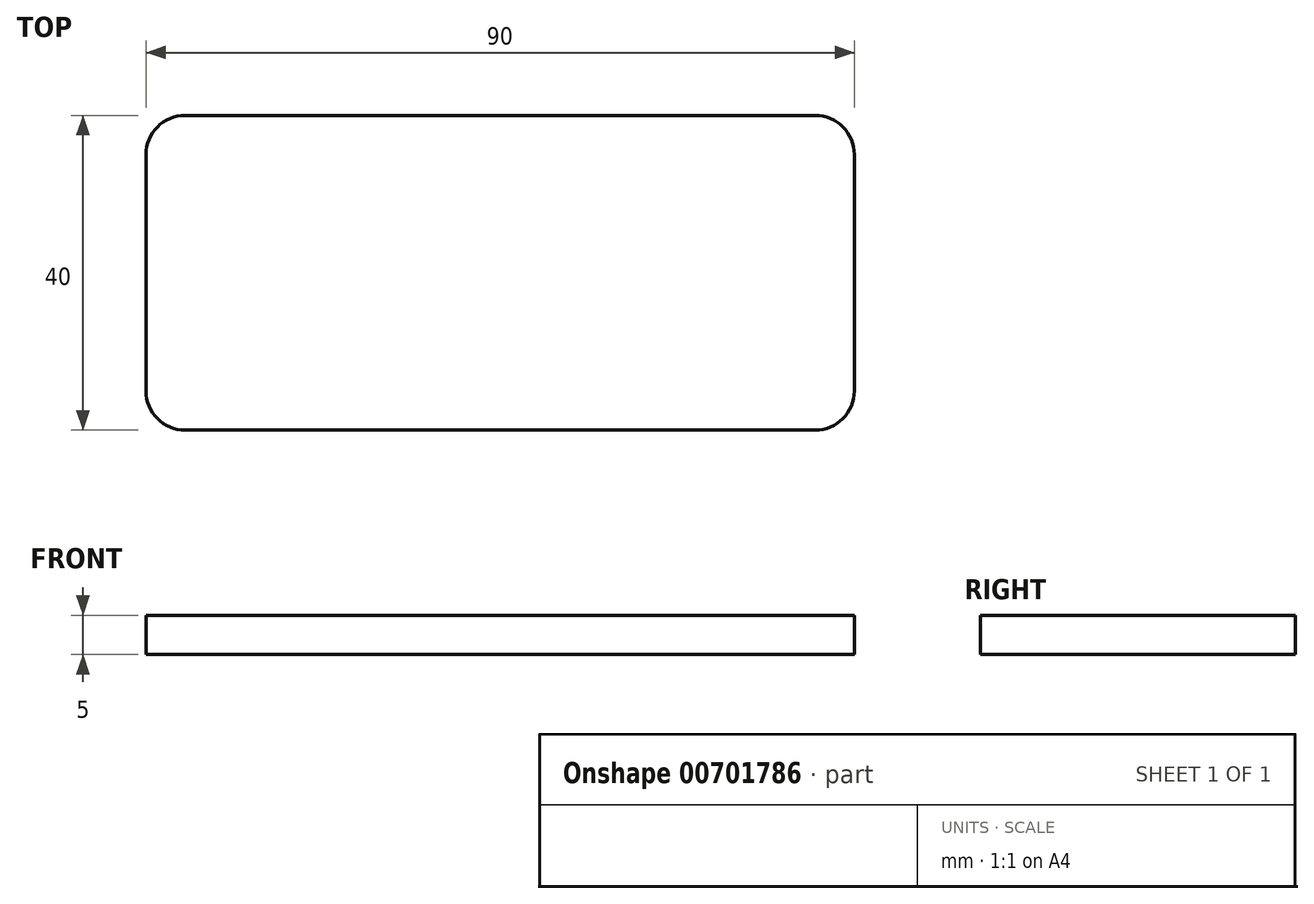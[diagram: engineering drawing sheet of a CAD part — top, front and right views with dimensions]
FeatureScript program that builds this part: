
annotation { "Feature Type Name" : "Feature", "Feature Type Description" : "" }
export const myFeature = defineFeature(function(context is Context, id is Id, definition is map)
    precondition{}
    {
        {
            var Q0;
            Q0=qCreatedBy(makeId("Top.planeOp"),FACE);
            var sketch = newSketch(context, id + "F0", { "sketchPlane" : qUnion([Q0])});
            skLineSegment(sketch, "E0.bottom", {"start": v(40, 20) * mm, "end": v(-40, 20) * mm});
            skLineSegment(sketch, "E0.top", {"start": v(40, -20) * mm, "end": v(-40, -20) * mm});
            skLineSegment(sketch, "E0.left", {"start": v(45, 15) * mm, "end": v(45, -15) * mm});
            skLineSegment(sketch, "E0.right", {"start": v(-45, 15) * mm, "end": v(-45, -15) * mm});
            skPoint(sketch, "E0.middle", {"position": v(0, 0) * mm});
            skPoint(sketch, "E1.visualSharp", {"position": v(-45, 20) * mm});
            skArc(sketch, "E1.filletArc", {"start": v(-40, 20) * mm, "mid": v(-43.54, 18.54) * mm, "end": v(-45, 15) * mm});
            skPoint(sketch, "E2.visualSharp", {"position": v(45, 20) * mm});
            skArc(sketch, "E2.filletArc", {"start": v(45, 15) * mm, "mid": v(43.54, 18.54) * mm, "end": v(40, 20) * mm});
            skPoint(sketch, "E3.visualSharp", {"position": v(45, -20) * mm});
            skArc(sketch, "E3.filletArc", {"start": v(40, -20) * mm, "mid": v(43.54, -18.54) * mm, "end": v(45, -15) * mm});
            skPoint(sketch, "E4.visualSharp", {"position": v(-45, -20) * mm});
            skArc(sketch, "E4.filletArc", {"start": v(-45, -15) * mm, "mid": v(-43.54, -18.54) * mm, "end": v(-40, -20) * mm});
            skSolve(sketch);
        }
        {
            var Q0;
            Q0 = qSketchRegion(id + "F0", true);
            extrude(context, id + "F1", {"entities" : qUnion([Q0]), "depth" : 5 * mm, "offsetDistance" : 25 * mm});
        }
    });
